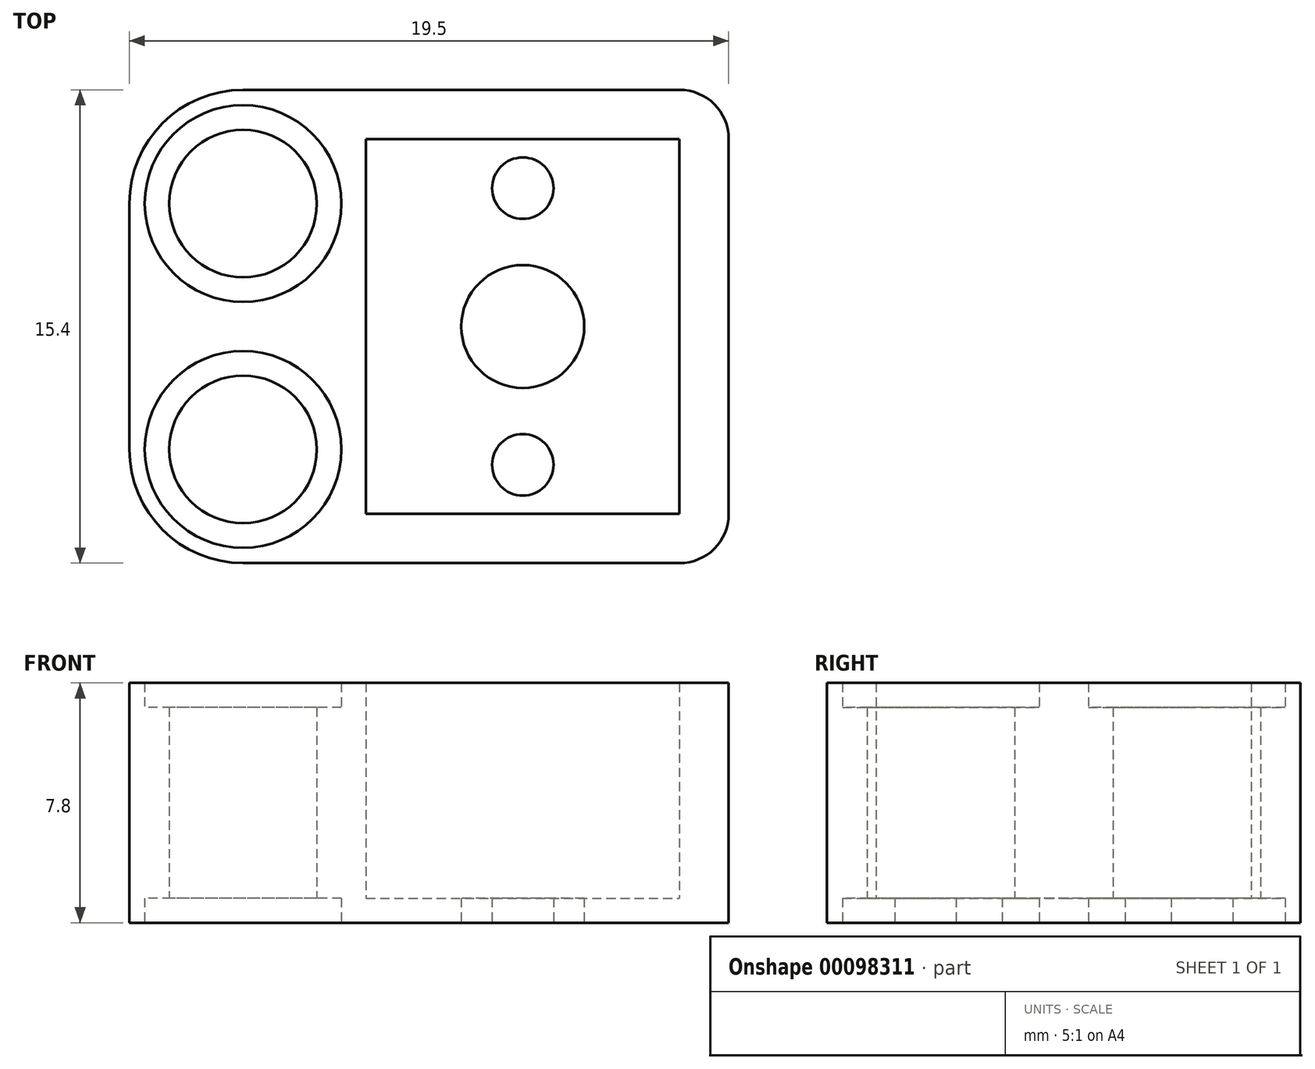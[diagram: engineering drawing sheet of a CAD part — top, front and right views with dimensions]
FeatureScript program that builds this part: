
annotation { "Feature Type Name" : "Feature", "Feature Type Description" : "" }
export const myFeature = defineFeature(function(context is Context, id is Id, definition is map)
    precondition{}
    {
        {
            var Q0;
            Q0=qCreatedBy(makeId("Top.planeOp"),FACE);
            var sketch = newSketch(context, id + "F0", { "sketchPlane" : qUnion([Q0])});
            skLineSegment(sketch, "E0.bottom", {"start": v(-9.1, 7.7) * mm, "end": v(5.1, 7.7) * mm});
            skLineSegment(sketch, "E0.top", {"start": v(-9.1, -7.7) * mm, "end": v(5.1, -7.7) * mm});
            skLineSegment(sketch, "E0.left", {"start": v(-12.8, 4) * mm, "end": v(-12.8, -4) * mm});
            skPoint(sketch, "E1.visualSharp", {"position": v(-12.8, -7.7) * mm});
            skArc(sketch, "E1.filletArc", {"start": v(-12.8, -4) * mm, "mid": v(-11.72, -6.62) * mm, "end": v(-9.1, -7.7) * mm});
            skPoint(sketch, "E2.visualSharp", {"position": v(-12.8, 7.7) * mm});
            skArc(sketch, "E2.filletArc", {"start": v(-9.1, 7.7) * mm, "mid": v(-11.72, 6.62) * mm, "end": v(-12.8, 4) * mm});
            skCircle(sketch, "E3", {"center": v(-9.1, 4) * mm, "radius": 3.2 * mm});
            skCircle(sketch, "E4", {"center": v(-9.1, 4) * mm, "radius": 2.4 * mm});
            skCircle(sketch, "E5", {"center": v(-9.1, -4) * mm, "radius": 2.4 * mm});
            skCircle(sketch, "E6", {"center": v(-9.1, -4) * mm, "radius": 3.2 * mm});
            skLineSegment(sketch, "E7.bottom", {"start": v(-5.1, 6.1) * mm, "end": v(5.1, 6.1) * mm});
            skLineSegment(sketch, "E7.top", {"start": v(-5.1, -6.1) * mm, "end": v(5.1, -6.1) * mm});
            skLineSegment(sketch, "E7.left", {"start": v(-5.1, 6.1) * mm, "end": v(-5.1, -6.1) * mm});
            skLineSegment(sketch, "E7.right", {"start": v(5.1, 6.1) * mm, "end": v(5.1, -6.1) * mm});
            skCircle(sketch, "E8", {"center": v(0, 0) * mm, "radius": 2 * mm});
            skCircle(sketch, "E9", {"center": v(0, 4.5) * mm, "radius": 1 * mm});
            skCircle(sketch, "E10", {"center": v(0, -4.5) * mm, "radius": 1 * mm});
            skLineSegment(sketch, "E11", {"start": v(6.7, 6.1) * mm, "end": v(6.7, -6.1) * mm});
            skPoint(sketch, "E12.visualSharp", {"position": v(6.7, 7.7) * mm});
            skArc(sketch, "E12.filletArc", {"start": v(6.7, 6.1) * mm, "mid": v(6.23, 7.23) * mm, "end": v(5.1, 7.7) * mm});
            skPoint(sketch, "E13.visualSharp", {"position": v(6.7, -7.7) * mm});
            skArc(sketch, "E13.filletArc", {"start": v(5.1, -7.7) * mm, "mid": v(6.23, -7.23) * mm, "end": v(6.7, -6.1) * mm});
            skSolve(sketch);
        }
        {
            var Q0;
            Q0=makeQuery(id+"F0.imprint","IMPRINT",FACE,{"disambiguationData":[TD([[makeQuery(id+"F0.imprint","IMPRINT",EDGE,{"derivedFrom":sQuery(id+"F0.wireOp",EDGE,"E0.bottom")}),-1.0]])]});
            extrude(context, id + "F1", {"entities" : qUnion([Q0]), "depth" : 7.8 * mm});
        }
        {
            var Q0;
            Q0=makeQuery(id+"F0.imprint","IMPRINT",FACE,{"disambiguationData":[TD([[makeQuery(id+"F0.imprint","IMPRINT",EDGE,{"derivedFrom":sQuery(id+"F0.wireOp",EDGE,"E5")}),-1.0]])]});
            var Q1;
            Q1=makeQuery(id+"F0.imprint","IMPRINT",FACE,{"disambiguationData":[TD([[makeQuery(id+"F0.imprint","IMPRINT",EDGE,{"derivedFrom":sQuery(id+"F0.wireOp",EDGE,"PKTqYszH-DR3T-vcPy-5sX4-L4kAaROeBFyM")}),-1.0]])]});
            var Q2;
            Q2=makeQuery(id+"F0.imprint","IMPRINT",FACE,{"disambiguationData":[TD([[makeQuery(id+"F0.imprint","IMPRINT",EDGE,{"derivedFrom":sQuery(id+"F0.wireOp",EDGE,"E3")}),1.0]])]});
            var Q3;
            Q3=makeQuery(id+"F0.imprint","IMPRINT",FACE,{"disambiguationData":[TD([[makeQuery(id+"F0.imprint","IMPRINT",EDGE,{"derivedFrom":sQuery(id+"F0.wireOp",EDGE,"9llju7xV-WvdD-dp10-O6V5-PlvfxY4rb5wI")}),-1.0]])]});
            extrude(context, id + "F2", {"entities" : qUnion([Q0, Q1, Q2, Q3]), "operationType" : NewBodyOperationType.ADD, "depth" : 7 * mm, "hasSecondDirection" : true, "secondDirectionOppositeDirection" : false, "secondDirectionDepth" : 0.8 * mm});
        }
        {
            var Q0;
            Q0=makeQuery(id+"F0.imprint","IMPRINT",FACE,{"disambiguationData":[TD([[makeQuery(id+"F0.imprint","IMPRINT",EDGE,{"derivedFrom":sQuery(id+"F0.wireOp",EDGE,"E7.bottom")}),-1.0]])]});
            extrude(context, id + "F3", {"entities" : qUnion([Q0]), "operationType" : NewBodyOperationType.ADD, "depth" : 0.8 * mm});
        }
    });
